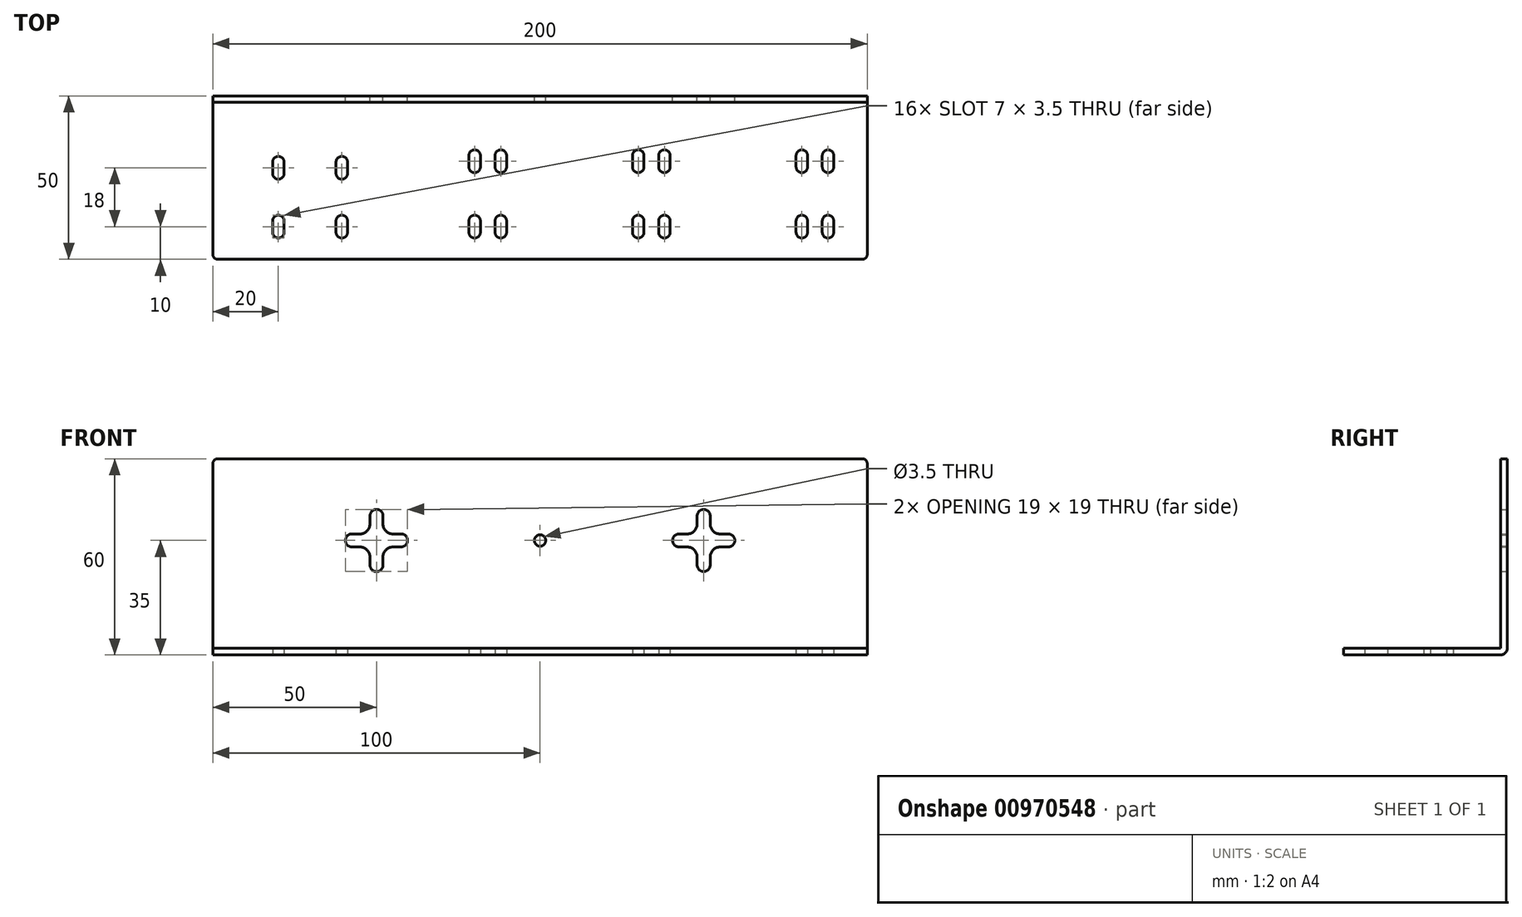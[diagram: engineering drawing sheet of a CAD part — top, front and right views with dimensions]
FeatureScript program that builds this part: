
annotation { "Feature Type Name" : "Feature", "Feature Type Description" : "" }
export const myFeature = defineFeature(function(context is Context, id is Id, definition is map)
    precondition{}
    {
        {
            var Q0;
            Q0=qCreatedBy(makeId("Right.planeOp"),FACE);
            var sketch = newSketch(context, id + "F0", { "sketchPlane" : qUnion([Q0])});
            skLineSegment(sketch, "E0", {"start": v(0, 0) * mm, "end": v(50, 0) * mm});
            skLineSegment(sketch, "E1", {"start": v(50, 0) * mm, "end": v(50, 60) * mm});
            skLineSegment(sketch, "E2.0", {"start": v(48, 2) * mm, "end": v(48, 60) * mm});
            skLineSegment(sketch, "E3.0", {"start": v(0, 2) * mm, "end": v(48, 2) * mm});
            skLineSegment(sketch, "E4", {"start": v(0, 2) * mm, "end": v(0, 0) * mm});
            skLineSegment(sketch, "E5", {"start": v(48, 60) * mm, "end": v(50, 60) * mm});
            skLineSegment(sketch, "E6.filletArc", {"start": v(48, 2) * mm, "end": v(48, 2) * mm});
            skSolve(sketch);
        }
        {
            var Q0;
            Q0 = qSketchRegion(id + "F0", true);
            extrude(context, id + "F1", {"entities" : qUnion([Q0]), "endBound" : BoundingType.SYMMETRIC, "depth" : 200 * mm, "offsetDistance" : 25 * mm});
        }
        {
            var Q0;
            Q0=makeQuery(id+"F1.opExtrude","SWEPT_FACE",FACE,{"disambiguationData":[OSD([sQuery(id+"F0.wireOp",EDGE,"E0")])]});
            var sketch = newSketch(context, id + "F2", { "sketchPlane" : qUnion([Q0])});
            skLineSegment(sketch, "E7.bottom", {"start": v(-62.35, -10) * mm, "end": v(-60.6, -10) * mm});
            skLineSegment(sketch, "E7.top", {"start": v(-80, -28) * mm, "end": v(-60.6, -28) * mm});
            skLineSegment(sketch, "E7.left", {"start": v(-80, -10) * mm, "end": v(-80, -11.75) * mm});
            skLineSegment(sketch, "E8.bottom", {"start": v(-18.25, -10) * mm, "end": v(-13.75, -10) * mm});
            skLineSegment(sketch, "E9.0", {"start": v(-10.25, -28.25) * mm, "end": v(-10.25, -31.75) * mm});
            skLineSegment(sketch, "E9.1", {"start": v(-20, -8.25) * mm, "end": v(-12, -8.25) * mm});
            skLineSegment(sketch, "E9.2", {"start": v(-21.75, -28.25) * mm, "end": v(-21.75, -31.75) * mm});
            skLineSegment(sketch, "E9.3", {"start": v(-20, -31.75) * mm, "end": v(-12, -31.75) * mm});
            skLineSegment(sketch, "E10.0", {"start": v(-18.25, -28.25) * mm, "end": v(-18.25, -31.75) * mm});
            skLineSegment(sketch, "E11.0", {"start": v(-13.75, -28.25) * mm, "end": v(-13.75, -31.75) * mm});
            skArc(sketch, "E12", {"start": v(-21.75, -11.75) * mm, "mid": v(-20, -13.5) * mm, "end": v(-18.25, -11.75) * mm});
            skArc(sketch, "E13", {"start": v(-13.75, -11.75) * mm, "mid": v(-12, -13.5) * mm, "end": v(-10.25, -11.75) * mm});
            skArc(sketch, "E14", {"start": v(-10.25, -28.25) * mm, "mid": v(-12, -26.5) * mm, "end": v(-13.75, -28.25) * mm});
            skArc(sketch, "E15", {"start": v(-18.25, -28.25) * mm, "mid": v(-20, -26.5) * mm, "end": v(-21.75, -28.25) * mm});
            skLineSegment(sketch, "E16.filletArc", {"start": v(-20, -8.25) * mm, "end": v(-20, -8.25) * mm});
            skPoint(sketch, "E17.newPointB", {"position": v(-12, -8.25) * mm});
            skLineSegment(sketch, "E17.filletArc", {"start": v(-12, -8.25) * mm, "end": v(-12, -8.25) * mm});
            skLineSegment(sketch, "E18.filletArc", {"start": v(-20, -31.75) * mm, "end": v(-20, -31.75) * mm});
            skArc(sketch, "E19", {"start": v(-18.25, -8.25) * mm, "mid": v(-20, -6.5) * mm, "end": v(-21.75, -8.25) * mm});
            skArc(sketch, "E20", {"start": v(-10.25, -8.25) * mm, "mid": v(-12, -6.5) * mm, "end": v(-13.75, -8.25) * mm});
            skArc(sketch, "E21", {"start": v(-21.75, -31.75) * mm, "mid": v(-20, -33.5) * mm, "end": v(-18.25, -31.75) * mm});
            skArc(sketch, "E22", {"start": v(-13.75, -31.75) * mm, "mid": v(-12, -33.5) * mm, "end": v(-10.25, -31.75) * mm});
            skLineSegment(sketch, "E23", {"start": v(-21.75, -8.25) * mm, "end": v(-21.75, -11.75) * mm});
            skLineSegment(sketch, "E24", {"start": v(-18.25, -8.25) * mm, "end": v(-18.25, -11.75) * mm});
            skLineSegment(sketch, "E25", {"start": v(-13.75, -8.25) * mm, "end": v(-13.75, -11.75) * mm});
            skLineSegment(sketch, "E26", {"start": v(-10.25, -8.25) * mm, "end": v(-10.25, -11.75) * mm});
            skLineSegment(sketch, "E27", {"start": v(-80, -10) * mm, "end": v(-80, -8.24) * mm});
            skLineSegment(sketch, "E28.filletArc", {"start": v(-46.75, -10.9) * mm, "end": v(-46.75, -10.9) * mm});
            skArc(sketch, "E29", {"start": v(-78.25, -8.25) * mm, "mid": v(-80, -6.5) * mm, "end": v(-81.75, -8.25) * mm});
            skArc(sketch, "E30", {"start": v(-81.75, -11.75) * mm, "mid": v(-80, -13.5) * mm, "end": v(-78.25, -11.75) * mm});
            skArc(sketch, "E31", {"start": v(-62.35, -11.75) * mm, "mid": v(-60.6, -13.5) * mm, "end": v(-58.85, -11.75) * mm});
            skArc(sketch, "E32", {"start": v(-58.85, -8.25) * mm, "mid": v(-60.6, -6.5) * mm, "end": v(-62.35, -8.25) * mm});
            skArc(sketch, "E33", {"start": v(-78.25, -26.25) * mm, "mid": v(-80, -24.5) * mm, "end": v(-81.75, -26.25) * mm});
            skArc(sketch, "E34", {"start": v(-58.85, -26.25) * mm, "mid": v(-60.6, -24.5) * mm, "end": v(-62.35, -26.25) * mm});
            skArc(sketch, "E35", {"start": v(-81.75, -29.75) * mm, "mid": v(-80, -31.5) * mm, "end": v(-78.25, -29.75) * mm});
            skArc(sketch, "E36", {"start": v(-62.35, -29.75) * mm, "mid": v(-60.6, -31.5) * mm, "end": v(-58.85, -29.75) * mm});
            skLineSegment(sketch, "E37", {"start": v(-81.75, -8.25) * mm, "end": v(-81.75, -11.75) * mm});
            skLineSegment(sketch, "E38.0", {"start": v(-78.25, -8.25) * mm, "end": v(-78.25, -11.75) * mm});
            skLineSegment(sketch, "E39.0", {"start": v(-58.85, -8.25) * mm, "end": v(-58.85, -11.75) * mm});
            skLineSegment(sketch, "E40.0", {"start": v(-62.35, -8.25) * mm, "end": v(-62.35, -11.75) * mm});
            skPoint(sketch, "E41.orphan", {"position": v(-21.75, -8.25) * mm});
            skPoint(sketch, "E42.orphan", {"position": v(-18.25, -8.25) * mm});
            skPoint(sketch, "E43.orphan", {"position": v(-13.75, -8.25) * mm});
            skLineSegment(sketch, "E44.trimOffspring", {"start": v(-81.75, -26.25) * mm, "end": v(-81.75, -29.75) * mm});
            skLineSegment(sketch, "E45.trimOffspring", {"start": v(-78.25, -26.25) * mm, "end": v(-78.25, -29.75) * mm});
            skLineSegment(sketch, "E46.trimOffspring", {"start": v(-62.35, -26.25) * mm, "end": v(-62.35, -29.75) * mm});
            skLineSegment(sketch, "E47.trimOffspring", {"start": v(-58.85, -26.25) * mm, "end": v(-58.85, -29.75) * mm});
            skLineSegment(sketch, "E48.trimOffspring", {"start": v(-80, -13.5) * mm, "end": v(-80, -24.5) * mm});
            skPoint(sketch, "E49.start.orphan", {"position": v(-12, -30) * mm});
            skLineSegment(sketch, "E50.1.0.0", {"start": v(39.75, -8.25) * mm, "end": v(39.75, -11.75) * mm});
            skArc(sketch, "E50.1.0.1", {"start": v(39.75, -28.25) * mm, "mid": v(38, -26.5) * mm, "end": v(36.25, -28.25) * mm});
            skArc(sketch, "E50.1.0.2", {"start": v(31.75, -28.25) * mm, "mid": v(30, -26.5) * mm, "end": v(28.25, -28.25) * mm});
            skLineSegment(sketch, "E50.1.0.3", {"start": v(30, -31.75) * mm, "end": v(38, -31.75) * mm});
            skPoint(sketch, "E50.1.0.4", {"position": v(38, -8.25) * mm});
            skArc(sketch, "E50.1.0.5", {"start": v(36.25, -11.75) * mm, "mid": v(38, -13.5) * mm, "end": v(39.75, -11.75) * mm});
            skPoint(sketch, "E50.1.0.6", {"position": v(38, -30) * mm});
            skArc(sketch, "E50.1.0.7", {"start": v(31.75, -8.25) * mm, "mid": v(30, -6.5) * mm, "end": v(28.25, -8.25) * mm});
            skLineSegment(sketch, "E50.1.0.8", {"start": v(28.25, -28.25) * mm, "end": v(28.25, -31.75) * mm});
            skLineSegment(sketch, "E50.1.0.9", {"start": v(31.75, -28.25) * mm, "end": v(31.75, -31.75) * mm});
            skLineSegment(sketch, "E50.1.0.10", {"start": v(39.75, -28.25) * mm, "end": v(39.75, -31.75) * mm});
            skLineSegment(sketch, "E50.1.0.11", {"start": v(31.75, -10) * mm, "end": v(36.25, -10) * mm});
            skArc(sketch, "E50.1.0.12", {"start": v(36.25, -31.75) * mm, "mid": v(38, -33.5) * mm, "end": v(39.75, -31.75) * mm});
            skPoint(sketch, "E50.1.0.13", {"position": v(31.75, -8.25) * mm});
            skArc(sketch, "E50.1.0.14", {"start": v(28.25, -11.75) * mm, "mid": v(30, -13.5) * mm, "end": v(31.75, -11.75) * mm});
            skLineSegment(sketch, "E50.1.0.15", {"start": v(36.25, -28.25) * mm, "end": v(36.25, -31.75) * mm});
            skPoint(sketch, "E50.1.0.16", {"position": v(36.25, -8.25) * mm});
            skArc(sketch, "E50.1.0.17", {"start": v(28.25, -31.75) * mm, "mid": v(30, -33.5) * mm, "end": v(31.75, -31.75) * mm});
            skLineSegment(sketch, "E50.1.0.18", {"start": v(28.25, -8.25) * mm, "end": v(28.25, -11.75) * mm});
            skPoint(sketch, "E50.1.0.19", {"position": v(28.25, -8.25) * mm});
            skArc(sketch, "E50.1.0.20", {"start": v(39.75, -8.25) * mm, "mid": v(38, -6.5) * mm, "end": v(36.25, -8.25) * mm});
            skLineSegment(sketch, "E50.1.0.21", {"start": v(31.75, -8.25) * mm, "end": v(31.75, -11.75) * mm});
            skLineSegment(sketch, "E50.1.0.22", {"start": v(36.25, -8.25) * mm, "end": v(36.25, -11.75) * mm});
            skLineSegment(sketch, "E50.1.0.23", {"start": v(30, -8.25) * mm, "end": v(38, -8.25) * mm});
            skLineSegment(sketch, "E50.2.0.0", {"start": v(89.75, -8.25) * mm, "end": v(89.75, -11.75) * mm});
            skArc(sketch, "E50.2.0.1", {"start": v(89.75, -28.25) * mm, "mid": v(88, -26.5) * mm, "end": v(86.25, -28.25) * mm});
            skArc(sketch, "E50.2.0.2", {"start": v(81.75, -28.25) * mm, "mid": v(80, -26.5) * mm, "end": v(78.25, -28.25) * mm});
            skLineSegment(sketch, "E50.2.0.3", {"start": v(80, -31.75) * mm, "end": v(88, -31.75) * mm});
            skPoint(sketch, "E50.2.0.4", {"position": v(88, -8.25) * mm});
            skArc(sketch, "E50.2.0.5", {"start": v(86.25, -11.75) * mm, "mid": v(88, -13.5) * mm, "end": v(89.75, -11.75) * mm});
            skPoint(sketch, "E50.2.0.6", {"position": v(88, -30) * mm});
            skArc(sketch, "E50.2.0.7", {"start": v(81.75, -8.25) * mm, "mid": v(80, -6.5) * mm, "end": v(78.25, -8.25) * mm});
            skLineSegment(sketch, "E50.2.0.8", {"start": v(78.25, -28.25) * mm, "end": v(78.25, -31.75) * mm});
            skLineSegment(sketch, "E50.2.0.9", {"start": v(81.75, -28.25) * mm, "end": v(81.75, -31.75) * mm});
            skLineSegment(sketch, "E50.2.0.10", {"start": v(89.75, -28.25) * mm, "end": v(89.75, -31.75) * mm});
            skLineSegment(sketch, "E50.2.0.11", {"start": v(81.75, -10) * mm, "end": v(86.25, -10) * mm});
            skArc(sketch, "E50.2.0.12", {"start": v(86.25, -31.75) * mm, "mid": v(88, -33.5) * mm, "end": v(89.75, -31.75) * mm});
            skPoint(sketch, "E50.2.0.13", {"position": v(81.75, -8.25) * mm});
            skArc(sketch, "E50.2.0.14", {"start": v(78.25, -11.75) * mm, "mid": v(80, -13.5) * mm, "end": v(81.75, -11.75) * mm});
            skLineSegment(sketch, "E50.2.0.15", {"start": v(86.25, -28.25) * mm, "end": v(86.25, -31.75) * mm});
            skPoint(sketch, "E50.2.0.16", {"position": v(86.25, -8.25) * mm});
            skArc(sketch, "E50.2.0.17", {"start": v(78.25, -31.75) * mm, "mid": v(80, -33.5) * mm, "end": v(81.75, -31.75) * mm});
            skLineSegment(sketch, "E50.2.0.18", {"start": v(78.25, -8.25) * mm, "end": v(78.25, -11.75) * mm});
            skPoint(sketch, "E50.2.0.19", {"position": v(78.25, -8.25) * mm});
            skArc(sketch, "E50.2.0.20", {"start": v(89.75, -8.25) * mm, "mid": v(88, -6.5) * mm, "end": v(86.25, -8.25) * mm});
            skLineSegment(sketch, "E50.2.0.21", {"start": v(81.75, -8.25) * mm, "end": v(81.75, -11.75) * mm});
            skLineSegment(sketch, "E50.2.0.22", {"start": v(86.25, -8.25) * mm, "end": v(86.25, -11.75) * mm});
            skLineSegment(sketch, "E50.2.0.23", {"start": v(80, -8.25) * mm, "end": v(88, -8.25) * mm});
            skLineSegment(sketch, "E50.direction1", {"start": v(-21.75, -31.75) * mm, "end": v(28.25, -31.75) * mm, "construction": true});
            skSolve(sketch);
        }
        {
            var Q0;
            {var subQ3=sQuery(id+"F2.wireOp",EDGE,"E12");Q0=makeQuery(id+"F2.imprint","IMPRINT",FACE,{"disambiguationData":[TD([[makeQuery(id+"F2.imprint","IMPRINT",EDGE,{"derivedFrom":subQ3}),1.0]])]});}
            var Q1;
            {var subQ2=sQuery(id+"F2.wireOp",EDGE,"E13");Q1=makeQuery(id+"F2.imprint","IMPRINT",FACE,{"disambiguationData":[TD([[makeQuery(id+"F2.imprint","IMPRINT",EDGE,{"derivedFrom":subQ2}),1.0]])]});}
            var Q2;
            Q2=makeQuery(id+"F2.imprint","IMPRINT",FACE,{"disambiguationData":[TD([[makeQuery(id+"F2.imprint","IMPRINT",EDGE,{"derivedFrom":sQuery(id+"F2.wireOp",EDGE,"E9.2")}),1.0]])]});
            var Q3;
            Q3=makeQuery(id+"F2.imprint","IMPRINT",FACE,{"disambiguationData":[TD([[makeQuery(id+"F2.imprint","IMPRINT",EDGE,{"derivedFrom":sQuery(id+"F2.wireOp",EDGE,"E9.0")}),-1.0]])]});
            var Q4;
            {var subQ1=sQuery(id+"F2.wireOp",EDGE,"E50.1.0.7");Q4=makeQuery(id+"F2.imprint","IMPRINT",FACE,{"disambiguationData":[TD([[makeQuery(id+"F2.imprint","IMPRINT",EDGE,{"derivedFrom":subQ1}),1.0]])]});}
            var Q5;
            Q5=makeQuery(id+"F2.imprint","IMPRINT",FACE,{"disambiguationData":[TD([[makeQuery(id+"F2.imprint","IMPRINT",EDGE,{"derivedFrom":sQuery(id+"F2.wireOp",EDGE,"E50.1.0.0")}),-1.0]])]});
            var Q6;
            Q6=makeQuery(id+"F2.imprint","IMPRINT",FACE,{"disambiguationData":[TD([[makeQuery(id+"F2.imprint","IMPRINT",EDGE,{"derivedFrom":sQuery(id+"F2.wireOp",EDGE,"E50.1.0.1")}),1.0]])]});
            var Q7;
            Q7=makeQuery(id+"F2.imprint","IMPRINT",FACE,{"disambiguationData":[TD([[makeQuery(id+"F2.imprint","IMPRINT",EDGE,{"derivedFrom":sQuery(id+"F2.wireOp",EDGE,"E50.1.0.2")}),1.0]])]});
            var Q8;
            {var subQ1=sQuery(id+"F2.wireOp",EDGE,"E50.2.0.7");Q8=makeQuery(id+"F2.imprint","IMPRINT",FACE,{"disambiguationData":[TD([[makeQuery(id+"F2.imprint","IMPRINT",EDGE,{"derivedFrom":subQ1}),1.0]])]});}
            var Q9;
            Q9=makeQuery(id+"F2.imprint","IMPRINT",FACE,{"disambiguationData":[TD([[makeQuery(id+"F2.imprint","IMPRINT",EDGE,{"derivedFrom":sQuery(id+"F2.wireOp",EDGE,"E50.2.0.0")}),-1.0]])]});
            var Q10;
            Q10=makeQuery(id+"F2.imprint","IMPRINT",FACE,{"disambiguationData":[TD([[makeQuery(id+"F2.imprint","IMPRINT",EDGE,{"derivedFrom":sQuery(id+"F2.wireOp",EDGE,"E50.2.0.2")}),1.0]])]});
            var Q11;
            Q11=makeQuery(id+"F2.imprint","IMPRINT",FACE,{"disambiguationData":[TD([[makeQuery(id+"F2.imprint","IMPRINT",EDGE,{"derivedFrom":sQuery(id+"F2.wireOp",EDGE,"E50.2.0.1")}),1.0]])]});
            var Q12;
            Q12=makeQuery(id+"F2.imprint","IMPRINT",FACE,{"disambiguationData":[TD([[makeQuery(id+"F2.imprint","IMPRINT",EDGE,{"derivedFrom":sQuery(id+"F2.wireOp",EDGE,"E29")}),1.0]])]});
            var Q13;
            {var subQ0=sQuery(id+"F2.wireOp",EDGE,"E35");Q13=makeQuery(id+"F2.imprint","IMPRINT",FACE,{"disambiguationData":[TD([[makeQuery(id+"F2.imprint","IMPRINT",EDGE,{"derivedFrom":subQ0}),1.0]])]});}
            var Q14;
            {var subQ1=sQuery(id+"F2.wireOp",EDGE,"E34");Q14=makeQuery(id+"F2.imprint","IMPRINT",FACE,{"disambiguationData":[TD([[makeQuery(id+"F2.imprint","IMPRINT",EDGE,{"derivedFrom":subQ1}),1.0]])]});}
            var Q15;
            {var subQ3=sQuery(id+"F2.wireOp",EDGE,"E31");Q15=makeQuery(id+"F2.imprint","IMPRINT",FACE,{"disambiguationData":[TD([[makeQuery(id+"F2.imprint","IMPRINT",EDGE,{"derivedFrom":subQ3}),1.0]])]});}
            extrude(context, id + "F3", {"entities" : qUnion([Q0, Q1, Q2, Q3, Q4, Q5, Q6, Q7, Q8, Q9, Q10, Q11, Q12, Q13, Q14, Q15]), "operationType" : NewBodyOperationType.REMOVE, "endBound" : BoundingType.THROUGH_ALL, "oppositeDirection" : true, "depth" : 25 * mm, "offsetDistance" : 25 * mm});
        }
        {
            var Q0;
            Q0=makeQuery(id+"F1.opExtrude","CAP_EDGE",EDGE,{"disambiguationData":[OSD([sQuery(id+"F0.wireOp",EDGE,"E4")])],"isStart":false});
            var Q1;
            Q1=makeQuery(id+"F1.opExtrude","CAP_EDGE",EDGE,{"disambiguationData":[OSD([sQuery(id+"F0.wireOp",EDGE,"E5")])],"isStart":false});
            var Q2;
            Q2=makeQuery(id+"F1.opExtrude","CAP_EDGE",EDGE,{"disambiguationData":[OSD([sQuery(id+"F0.wireOp",EDGE,"E4")])],"isStart":true});
            var Q3;
            Q3=makeQuery(id+"F1.opExtrude","CAP_EDGE",EDGE,{"disambiguationData":[OSD([sQuery(id+"F0.wireOp",EDGE,"E5")])],"isStart":true});
            fillet(context, id + "F4", {"entities" : qUnion([Q0, Q1, Q2, Q3]), "radius" : 1.5 * mm, "tangentPropagation" : true, "allowEdgeOverflow" : false});
        }
        {
            var Q0;
            Q0=makeQuery(id+"F1.opExtrude","SWEPT_EDGE",EDGE,{"disambiguationData":[OSD([sQuery(id+"F0.wireOp",EDGE,"E0"),sQuery(id+"F0.wireOp",EDGE,"E1")])]});
            fillet(context, id + "F5", {"entities" : qUnion([Q0]), "radius" : 2 * mm, "tangentPropagation" : true, "allowEdgeOverflow" : false});
        }
        {
            var Q0;
            Q0=makeQuery(id+"F1.opExtrude","SWEPT_FACE",FACE,{"disambiguationData":[OSD([sQuery(id+"F0.wireOp",EDGE,"E1")])]});
            var sketch = newSketch(context, id + "F6", { "sketchPlane" : qUnion([Q0])});
            skCircle(sketch, "E51", {"center": v(0, 35) * mm, "radius": 1.75 * mm});
            skLineSegment(sketch, "E52", {"start": v(-42.5, 35) * mm, "end": v(-57.5, 35) * mm});
            skLineSegment(sketch, "E53", {"start": v(-50, 27.5) * mm, "end": v(-50, 42.5) * mm});
            skArc(sketch, "E54.0.startCap", {"start": v(-48, 27.5) * mm, "mid": v(-50, 25.5) * mm, "end": v(-52, 27.5) * mm});
            skArc(sketch, "E54.0.endCap", {"start": v(-52, 42.5) * mm, "mid": v(-50, 44.5) * mm, "end": v(-48, 42.5) * mm});
            skLineSegment(sketch, "E54.0.left", {"start": v(-52, 27.5) * mm, "end": v(-52, 42.5) * mm});
            skLineSegment(sketch, "E54.0.right", {"start": v(-48, 27.5) * mm, "end": v(-48, 42.5) * mm});
            skArc(sketch, "E54.1.startCap", {"start": v(-42.5, 37) * mm, "mid": v(-40.5, 35) * mm, "end": v(-42.5, 33) * mm});
            skArc(sketch, "E54.1.endCap", {"start": v(-57.5, 33) * mm, "mid": v(-59.5, 35) * mm, "end": v(-57.5, 37) * mm});
            skLineSegment(sketch, "E54.1.left", {"start": v(-42.5, 33) * mm, "end": v(-57.5, 33) * mm});
            skLineSegment(sketch, "E54.1.right", {"start": v(-42.5, 37) * mm, "end": v(-57.5, 37) * mm});
            skLineSegment(sketch, "E55.1.0.0", {"start": v(52, 27.5) * mm, "end": v(52, 42.5) * mm});
            skLineSegment(sketch, "E55.1.0.1", {"start": v(48, 27.5) * mm, "end": v(48, 42.5) * mm});
            skLineSegment(sketch, "E55.1.0.2", {"start": v(50, 27.5) * mm, "end": v(50, 42.5) * mm});
            skLineSegment(sketch, "E55.1.0.3", {"start": v(57.5, 35) * mm, "end": v(42.5, 35) * mm});
            skLineSegment(sketch, "E55.1.0.4", {"start": v(57.5, 33) * mm, "end": v(42.5, 33) * mm});
            skLineSegment(sketch, "E55.1.0.5", {"start": v(57.5, 37) * mm, "end": v(42.5, 37) * mm});
            skArc(sketch, "E55.1.0.6", {"start": v(57.5, 37) * mm, "mid": v(59.5, 35) * mm, "end": v(57.5, 33) * mm});
            skArc(sketch, "E55.1.0.7", {"start": v(42.5, 33) * mm, "mid": v(40.5, 35) * mm, "end": v(42.5, 37) * mm});
            skArc(sketch, "E55.1.0.8", {"start": v(52, 27.5) * mm, "mid": v(50, 25.5) * mm, "end": v(48, 27.5) * mm});
            skArc(sketch, "E55.1.0.9", {"start": v(48, 42.5) * mm, "mid": v(50, 44.5) * mm, "end": v(52, 42.5) * mm});
            skLineSegment(sketch, "E55.2.0.0", {"start": v(152, 27.5) * mm, "end": v(152, 42.5) * mm});
            skLineSegment(sketch, "E55.2.0.1", {"start": v(148, 27.5) * mm, "end": v(148, 42.5) * mm});
            skLineSegment(sketch, "E55.2.0.2", {"start": v(150, 27.5) * mm, "end": v(150, 42.5) * mm});
            skLineSegment(sketch, "E55.2.0.3", {"start": v(157.5, 35) * mm, "end": v(142.5, 35) * mm});
            skLineSegment(sketch, "E55.2.0.4", {"start": v(157.5, 33) * mm, "end": v(142.5, 33) * mm});
            skLineSegment(sketch, "E55.2.0.5", {"start": v(157.5, 37) * mm, "end": v(142.5, 37) * mm});
            skArc(sketch, "E55.2.0.6", {"start": v(157.5, 37) * mm, "mid": v(159.5, 35) * mm, "end": v(157.5, 33) * mm});
            skArc(sketch, "E55.2.0.7", {"start": v(142.5, 33) * mm, "mid": v(140.5, 35) * mm, "end": v(142.5, 37) * mm});
            skArc(sketch, "E55.2.0.8", {"start": v(152, 27.5) * mm, "mid": v(150, 25.5) * mm, "end": v(148, 27.5) * mm});
            skArc(sketch, "E55.2.0.9", {"start": v(148, 42.5) * mm, "mid": v(150, 44.5) * mm, "end": v(152, 42.5) * mm});
            skLineSegment(sketch, "E55.direction1", {"start": v(-52, 27.5) * mm, "end": v(48, 27.5) * mm, "construction": true});
            skSolve(sketch);
        }
        {
            var Q0;
            Q0 = qSketchRegion(id + "F6", true);
            extrude(context, id + "F7", {"entities" : qUnion([Q0]), "operationType" : NewBodyOperationType.REMOVE, "oppositeDirection" : true, "depth" : 2 * mm, "offsetDistance" : 25 * mm});
        }
        {
            var Q0;
            Q0=makeQuery(id+"F7.boolean.opBoolean","COPY",EDGE,{"derivedFrom":makeQuery(id+"F7.opExtrude","SWEPT_EDGE",EDGE,{"disambiguationData":[OSD([sQuery(id+"F6.wireOp",EDGE,"E54.0.left"),sQuery(id+"F6.wireOp",EDGE,"E54.1.left")])]})});
            var Q1;
            Q1=makeQuery(id+"F7.boolean.opBoolean","COPY",EDGE,{"derivedFrom":makeQuery(id+"F7.opExtrude","SWEPT_EDGE",EDGE,{"disambiguationData":[OSD([sQuery(id+"F6.wireOp",EDGE,"E54.0.right"),sQuery(id+"F6.wireOp",EDGE,"E54.1.left")])]})});
            var Q2;
            Q2=makeQuery(id+"F7.boolean.opBoolean","COPY",EDGE,{"derivedFrom":makeQuery(id+"F7.opExtrude","SWEPT_EDGE",EDGE,{"disambiguationData":[OSD([sQuery(id+"F6.wireOp",EDGE,"E54.0.right"),sQuery(id+"F6.wireOp",EDGE,"E54.1.right")])]})});
            var Q3;
            Q3=makeQuery(id+"F7.boolean.opBoolean","COPY",EDGE,{"derivedFrom":makeQuery(id+"F7.opExtrude","SWEPT_EDGE",EDGE,{"disambiguationData":[OSD([sQuery(id+"F6.wireOp",EDGE,"E54.0.left"),sQuery(id+"F6.wireOp",EDGE,"E54.1.right")])]})});
            var Q4;
            Q4=makeQuery(id+"F7.boolean.opBoolean","COPY",EDGE,{"derivedFrom":makeQuery(id+"F7.opExtrude","SWEPT_EDGE",EDGE,{"disambiguationData":[OSD([sQuery(id+"F6.wireOp",EDGE,"E55.1.0.0"),sQuery(id+"F6.wireOp",EDGE,"E55.1.0.4")])]})});
            var Q5;
            Q5=makeQuery(id+"F7.boolean.opBoolean","COPY",EDGE,{"derivedFrom":makeQuery(id+"F7.opExtrude","SWEPT_EDGE",EDGE,{"disambiguationData":[OSD([sQuery(id+"F6.wireOp",EDGE,"E55.1.0.0"),sQuery(id+"F6.wireOp",EDGE,"E55.1.0.5")])]})});
            var Q6;
            Q6=makeQuery(id+"F7.boolean.opBoolean","COPY",EDGE,{"derivedFrom":makeQuery(id+"F7.opExtrude","SWEPT_EDGE",EDGE,{"disambiguationData":[OSD([sQuery(id+"F6.wireOp",EDGE,"E55.1.0.1"),sQuery(id+"F6.wireOp",EDGE,"E55.1.0.5")])]})});
            var Q7;
            Q7=makeQuery(id+"F7.boolean.opBoolean","COPY",EDGE,{"derivedFrom":makeQuery(id+"F7.opExtrude","SWEPT_EDGE",EDGE,{"disambiguationData":[OSD([sQuery(id+"F6.wireOp",EDGE,"E55.1.0.1"),sQuery(id+"F6.wireOp",EDGE,"E55.1.0.4")])]})});
            fillet(context, id + "F8", {"entities" : qUnion([Q0, Q1, Q2, Q3, Q4, Q5, Q6, Q7]), "radius" : 3 * mm, "tangentPropagation" : true, "allowEdgeOverflow" : false});
        }
    });
